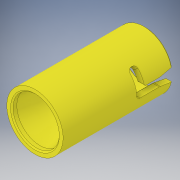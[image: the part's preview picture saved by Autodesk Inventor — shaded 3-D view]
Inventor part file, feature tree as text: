
AUTODESK INVENTOR PART (.ipt)
format: ipt  version: 2019 (Build 230136000, 136)  size: 717,312 bytes
history: native  units: mm
features: other x6, sketch x4, fillet x3, chamfer x3, extrude x2, pattern_circular x1
ambient origin geometry x8: Origin, YZ Plane, XZ Plane, XY Plane, X Axis, Y Axis, Z Axis, Center Point
bodies: Solide1 (feature_tree)
feature tree (19):
  other  "Révolution1"
  other  "Plan de construction2"
  extrude  "Extrusion1"  Depth=45.0mm
  other  "Hélicoïde1"
  extrude  "Extrusion2"  Depth=4.0mm
  fillet  "Congé1"  Radius=0.25mm
  fillet  "Congé2"  Radius=0.5mm
  fillet  "Congé3"  Radius=0.2mm
  chamfer  "Chanfrein1"  Angle=45.0deg  [1 undecoded]
  chamfer  "Chanfrein2"  Distance=22.0mm
  chamfer  "Chanfrein3"  Distance=0.25mm
  pattern_circular  "Réseau circulaire1"  [2 undecoded]
  sketch  "Esquisse1"
  sketch  "Esquisse2"
  sketch  "Esquisse3"
  sketch  "Esquisse4"
  other  "Projeter les arêtes coupées1"
  other  "Projeter les arêtes coupées2"
  other  "Projeter les arêtes coupées3"
note: 3 required parameter values undecoded (feature->parameter linkage not recoverable at this tier; creation-order binding heuristic only, values carry confidence <= 0.55)
